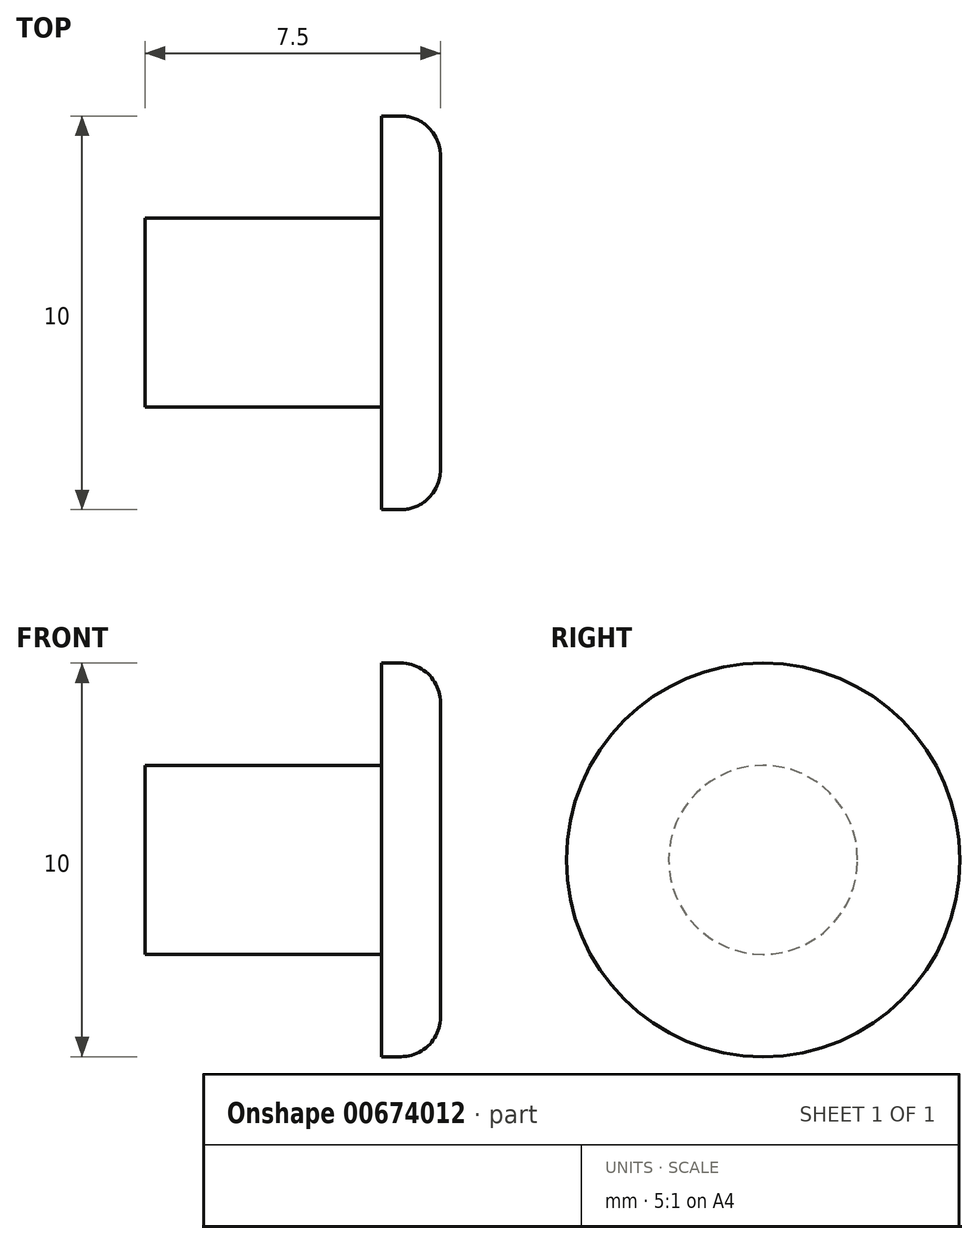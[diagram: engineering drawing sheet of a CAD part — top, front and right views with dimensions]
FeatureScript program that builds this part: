
annotation { "Feature Type Name" : "Feature", "Feature Type Description" : "" }
export const myFeature = defineFeature(function(context is Context, id is Id, definition is map)
    precondition{}
    {
        {
            var Q0;
            Q0=qCreatedBy(makeId("Right.planeOp"),FACE);
            var sketch = newSketch(context, id + "F0", { "sketchPlane" : qUnion([Q0])});
            skCircle(sketch, "E0", {"center": v(0, 0) * mm, "radius": 5 * mm});
            skSolve(sketch);
        }
        {
            var Q0;
            Q0=makeQuery(id+"F0.imprint","IMPRINT",FACE,{"disambiguationData":[TD([[makeQuery(id+"F0.imprint","IMPRINT",EDGE,{"derivedFrom":sQuery(id+"F0.wireOp",EDGE,"E0")}),1.0]])]});
            extrude(context, id + "F1", {"entities" : qUnion([Q0]), "oppositeDirection" : true, "depth" : 1.5 * mm, "offsetDistance" : 25 * mm});
        }
        {
            var Q0;
            Q0=makeQuery(id+"F1.opExtrude","CAP_EDGE",EDGE,{"disambiguationData":[OSD([sQuery(id+"F0.wireOp",EDGE,"E0")])],"isStart":true});
            fillet(context, id + "F2", {"entities" : qUnion([Q0]), "radius" : 1 * mm, "tangentPropagation" : true, "allowEdgeOverflow" : false});
        }
        {
            var Q0;
            Q0=makeQuery(id+"F1.opExtrude","CAP_FACE",FACE,{"disambiguationData":[OSD([sQuery(id+"F0.wireOp",EDGE,"E0")])],"isStart":false});
            var sketch = newSketch(context, id + "F3", { "sketchPlane" : qUnion([Q0])});
            skCircle(sketch, "E1", {"center": v(0, 0) * mm, "radius": 2.4 * mm});
            skSolve(sketch);
        }
        {
            var Q0;
            Q0=makeQuery(id+"F3.imprint","IMPRINT",FACE,{"disambiguationData":[TD([[makeQuery(id+"F3.imprint","IMPRINT",EDGE,{"derivedFrom":sQuery(id+"F3.wireOp",EDGE,"E1")}),1.0]])]});
            extrude(context, id + "F4", {"entities" : qUnion([Q0]), "operationType" : NewBodyOperationType.ADD, "depth" : 6 * mm, "offsetDistance" : 25 * mm});
        }
    });
